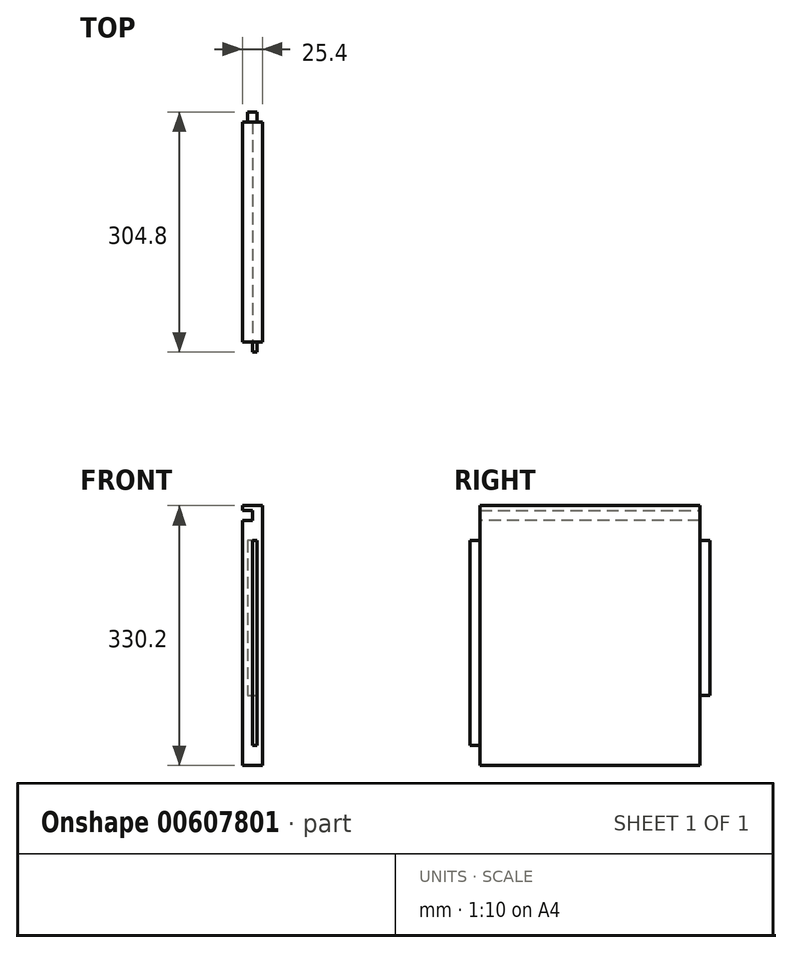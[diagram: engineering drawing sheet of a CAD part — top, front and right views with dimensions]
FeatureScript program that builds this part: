
annotation { "Feature Type Name" : "Feature", "Feature Type Description" : "" }
export const myFeature = defineFeature(function(context is Context, id is Id, definition is map)
    precondition{}
    {
        {
            var Q0;
            Q0=qCreatedBy(makeId("Right.planeOp"),FACE);
            var sketch = newSketch(context, id + "F0", { "sketchPlane" : qUnion([Q0])});
            skLineSegment(sketch, "E0.bottom", {"start": v(0, 0) * mm, "end": v(-279.4, 0) * mm});
            skLineSegment(sketch, "E0.top", {"start": v(0, 304.8) * mm, "end": v(-279.4, 304.8) * mm});
            skLineSegment(sketch, "E0.left", {"start": v(0, 0) * mm, "end": v(0, 304.8) * mm});
            skLineSegment(sketch, "E0.right", {"start": v(-279.4, 0) * mm, "end": v(-279.4, 304.8) * mm});
            skSolve(sketch);
        }
        {
            var Q0;
            Q0=makeQuery(id+"F0.imprint","IMPRINT",FACE,{"disambiguationData":[TD([[makeQuery(id+"F0.imprint","IMPRINT",EDGE,{"derivedFrom":sQuery(id+"F0.wireOp",EDGE,"E0.bottom")}),-1.0]])]});
            extrude(context, id + "F1", {"entities" : qUnion([Q0]), "depth" : 25.4 * mm, "offsetDistance" : 25.4 * mm});
        }
        {
            var Q0;
            Q0=qCreatedBy(makeId("Right.planeOp"),FACE);
            var sketch = newSketch(context, id + "F2", { "sketchPlane" : qUnion([Q0])});
            skLineSegment(sketch, "E1.bottom", {"start": v(0, 0) * mm, "end": v(-279.4, 0) * mm});
            skLineSegment(sketch, "E1.top", {"start": v(0, -25.4) * mm, "end": v(-279.4, -25.4) * mm});
            skLineSegment(sketch, "E1.left", {"start": v(0, 0) * mm, "end": v(0, -25.4) * mm});
            skLineSegment(sketch, "E1.right", {"start": v(-279.4, 0) * mm, "end": v(-279.4, -25.4) * mm});
            skSolve(sketch);
        }
        {
            var Q0;
            Q0=makeQuery(id+"F2.imprint","IMPRINT",FACE,{"disambiguationData":[TD([[makeQuery(id+"F2.imprint","IMPRINT",EDGE,{"derivedFrom":sQuery(id+"F2.wireOp",EDGE,"E1.bottom")}),1.0]])]});
            extrude(context, id + "F3", {"entities" : qUnion([Q0]), "operationType" : NewBodyOperationType.ADD, "depth" : 25.4 * mm, "offsetDistance" : 25.4 * mm});
        }
        {
            var Q0;
            Q0=makeQuery(id+"F3.boolean.opBoolean","MERGE",FACE,{"derivedFrom":[makeQuery(id+"F1.opExtrude","CAP_FACE",FACE,{"disambiguationData":[OSD([sQuery(id+"F0.wireOp",EDGE,"E0.bottom"),sQuery(id+"F0.wireOp",EDGE,"E0.top"),sQuery(id+"F0.wireOp",EDGE,"E0.left"),sQuery(id+"F0.wireOp",EDGE,"E0.right")])],"isStart":true}),makeQuery(id+"F3.opExtrude","CAP_FACE",FACE,{"disambiguationData":[OSD([sQuery(id+"F2.wireOp",EDGE,"E1.bottom"),sQuery(id+"F2.wireOp",EDGE,"E1.top"),sQuery(id+"F2.wireOp",EDGE,"E1.left"),sQuery(id+"F2.wireOp",EDGE,"E1.right")])],"isStart":true})]});
            var sketch = newSketch(context, id + "F4", { "sketchPlane" : qUnion([Q0])});
            skLineSegment(sketch, "E2", {"start": v(0, 304.8) * mm, "end": v(0, 298.45) * mm});
            skLineSegment(sketch, "E3", {"start": v(0, 298.45) * mm, "end": v(0, 285.75) * mm});
            skLineSegment(sketch, "E4", {"start": v(0, 285.75) * mm, "end": v(279.4, 285.75) * mm});
            skLineSegment(sketch, "E5", {"start": v(279.4, 285.75) * mm, "end": v(279.4, 298.45) * mm});
            skLineSegment(sketch, "E6", {"start": v(279.4, 298.45) * mm, "end": v(0, 298.45) * mm});
            skSolve(sketch);
        }
        {
            var Q0;
            Q0=makeQuery(id+"F4.imprint","IMPRINT",FACE,{"disambiguationData":[TD([[makeQuery(id+"F4.imprint","IMPRINT",EDGE,{"derivedFrom":sQuery(id+"F4.wireOp",EDGE,"E3")}),-1.0]])]});
            extrude(context, id + "F5", {"entities" : qUnion([Q0]), "operationType" : NewBodyOperationType.REMOVE, "oppositeDirection" : true, "depth" : 12.7 * mm, "offsetDistance" : 25.4 * mm});
        }
        {
            var Q0;
            Q0=makeQuery(id+"F3.boolean.opBoolean","MERGE",FACE,{"derivedFrom":[makeQuery(id+"F1.opExtrude","SWEPT_FACE",FACE,{"disambiguationData":[OSD([sQuery(id+"F0.wireOp",EDGE,"E0.right")])]}),makeQuery(id+"F3.opExtrude","SWEPT_FACE",FACE,{"disambiguationData":[OSD([sQuery(id+"F2.wireOp",EDGE,"E1.right")])]})]});
            var sketch = newSketch(context, id + "F6", { "sketchPlane" : qUnion([Q0])});
            skLineSegment(sketch, "E7", {"start": v(25.4, 304.8) * mm, "end": v(25.4, 260.35) * mm});
            skLineSegment(sketch, "E8", {"start": v(25.4, 260.35) * mm, "end": v(19.05, 260.35) * mm});
            skLineSegment(sketch, "E9", {"start": v(19.05, 260.35) * mm, "end": v(12.7, 260.35) * mm});
            skLineSegment(sketch, "E10", {"start": v(12.7, 260.35) * mm, "end": v(12.7, 0) * mm});
            skLineSegment(sketch, "E11", {"start": v(12.7, 0) * mm, "end": v(19.05, 0) * mm});
            skLineSegment(sketch, "E12", {"start": v(19.05, 0) * mm, "end": v(19.05, 260.35) * mm});
            skSolve(sketch);
        }
        {
            var Q0;
            Q0=makeQuery(id+"F6.imprint","IMPRINT",FACE,{"disambiguationData":[TD([[makeQuery(id+"F6.imprint","IMPRINT",EDGE,{"derivedFrom":sQuery(id+"F6.wireOp",EDGE,"E9")}),1.0]])]});
            extrude(context, id + "F7", {"entities" : qUnion([Q0]), "operationType" : NewBodyOperationType.ADD, "depth" : 12.7 * mm, "offsetDistance" : 25.4 * mm});
        }
        {
            var Q0;
            Q0=makeQuery(id+"F3.boolean.opBoolean","MERGE",FACE,{"derivedFrom":[makeQuery(id+"F1.opExtrude","SWEPT_FACE",FACE,{"disambiguationData":[OSD([sQuery(id+"F0.wireOp",EDGE,"E0.left")])]}),makeQuery(id+"F3.opExtrude","SWEPT_FACE",FACE,{"disambiguationData":[OSD([sQuery(id+"F2.wireOp",EDGE,"E1.left")])]})]});
            var sketch = newSketch(context, id + "F8", { "sketchPlane" : qUnion([Q0])});
            skLineSegment(sketch, "E13", {"start": v(-25.4, 304.8) * mm, "end": v(-25.4, 260.35) * mm});
            skLineSegment(sketch, "E14", {"start": v(-25.4, 260.35) * mm, "end": v(-19.05, 260.35) * mm});
            skLineSegment(sketch, "E15", {"start": v(-19.05, 260.35) * mm, "end": v(-6.35, 260.35) * mm});
            skLineSegment(sketch, "E16", {"start": v(-6.35, 260.35) * mm, "end": v(-6.35, 63.5) * mm});
            skLineSegment(sketch, "E17", {"start": v(-6.35, 63.5) * mm, "end": v(-19.05, 63.5) * mm});
            skLineSegment(sketch, "E18", {"start": v(-19.05, 63.5) * mm, "end": v(-19.05, 260.35) * mm});
            skSolve(sketch);
        }
        {
            var Q0;
            Q0=makeQuery(id+"F8.imprint","IMPRINT",FACE,{"disambiguationData":[TD([[makeQuery(id+"F8.imprint","IMPRINT",EDGE,{"derivedFrom":sQuery(id+"F8.wireOp",EDGE,"E15")}),-1.0]])]});
            extrude(context, id + "F9", {"entities" : qUnion([Q0]), "operationType" : NewBodyOperationType.ADD, "depth" : 12.7 * mm, "offsetDistance" : 25.4 * mm});
        }
    });
